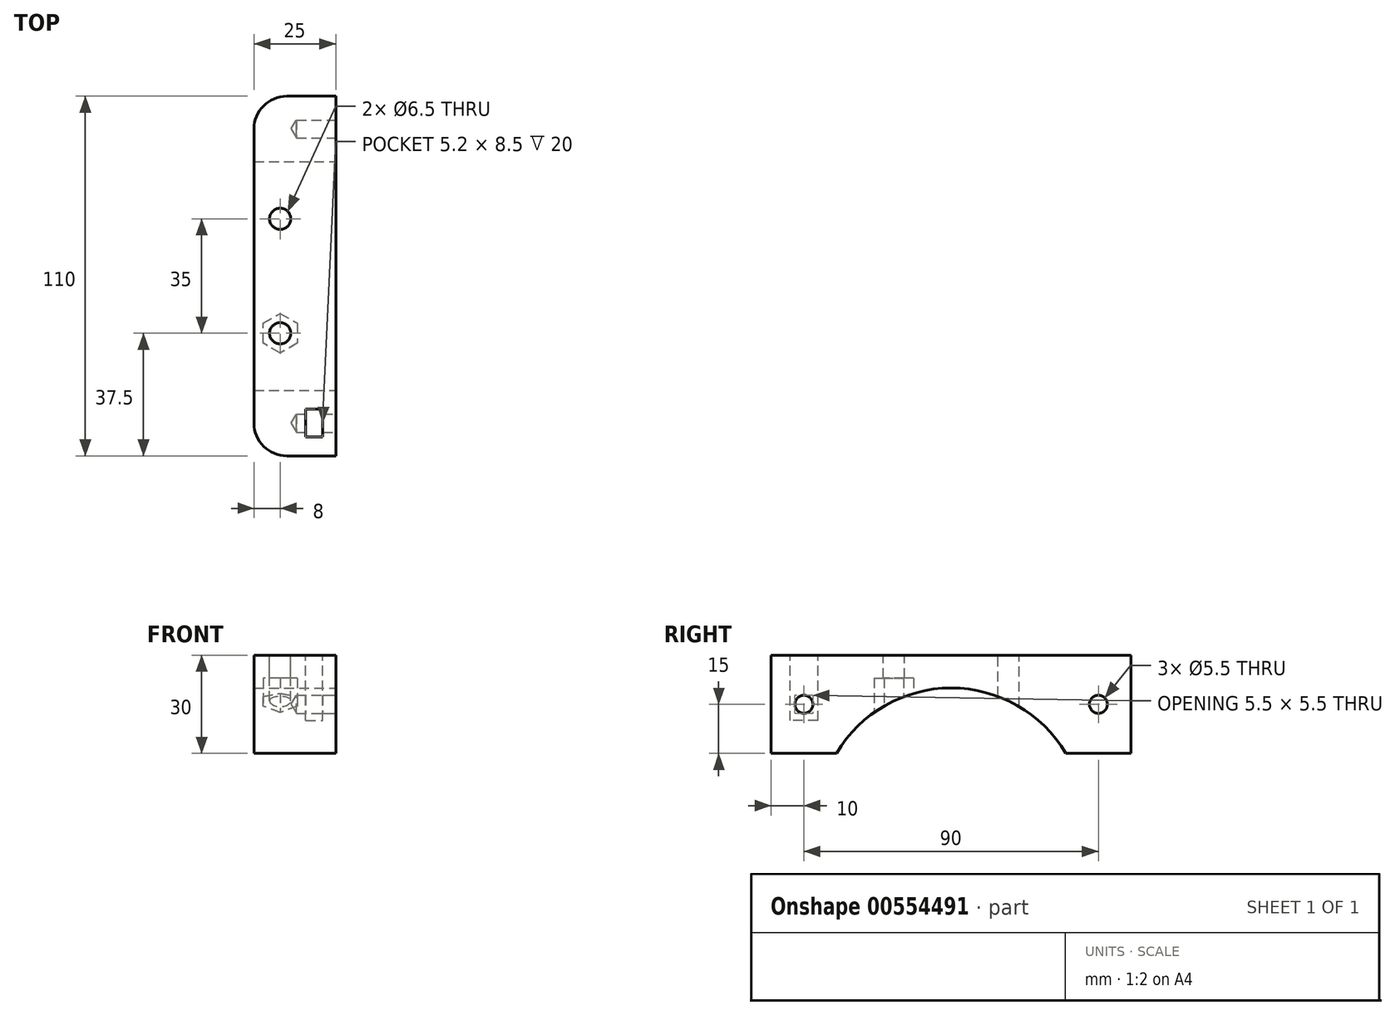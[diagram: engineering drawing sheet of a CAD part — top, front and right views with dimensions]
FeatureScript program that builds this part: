
annotation { "Feature Type Name" : "Feature", "Feature Type Description" : "" }
export const myFeature = defineFeature(function(context is Context, id is Id, definition is map)
    precondition{}
    {
        {
            var Q0;
            Q0=qCreatedBy(makeId("Right.planeOp"),FACE);
            var sketch = newSketch(context, id + "F0", { "sketchPlane" : qUnion([Q0])});
            skLineSegment(sketch, "E0.bottom", {"start": v(-55, 0) * mm, "end": v(55, 0) * mm});
            skLineSegment(sketch, "E0.top", {"start": v(-55, 30) * mm, "end": v(55, 30) * mm});
            skLineSegment(sketch, "E0.left", {"start": v(-55, 0) * mm, "end": v(-55, 30) * mm});
            skLineSegment(sketch, "E0.right", {"start": v(55, 0) * mm, "end": v(55, 30) * mm});
            skSolve(sketch);
        }
        {
            var Q0;
            Q0=makeQuery(id+"F0.imprint","IMPRINT",FACE,{"disambiguationData":[TD([[makeQuery(id+"F0.imprint","IMPRINT",EDGE,{"derivedFrom":sQuery(id+"F0.wireOp",EDGE,"E0.bottom")}),1.0]])]});
            extrude(context, id + "F1", {"entities" : qUnion([Q0]), "endBound" : BoundingType.SYMMETRIC, "depth" : 25 * mm, "offsetDistance" : 25 * mm});
        }
        {
            var Q0;
            Q0=makeQuery(id+"F1.opExtrude","CAP_FACE",FACE,{"disambiguationData":[OSD([sQuery(id+"F0.wireOp",EDGE,"E0.bottom"),sQuery(id+"F0.wireOp",EDGE,"E0.top"),sQuery(id+"F0.wireOp",EDGE,"E0.left"),sQuery(id+"F0.wireOp",EDGE,"E0.right")])],"isStart":false});
            var sketch = newSketch(context, id + "F2", { "sketchPlane" : qUnion([Q0])});
            skPoint(sketch, "E1", {"position": v(-45, 15) * mm});
            skPoint(sketch, "E2", {"position": v(45, 15) * mm});
            skSolve(sketch);
        }
        {
            var Q0;
            Q0=sQuery(id+"F2.wireOp",VERTEX,"E1");
            var Q1;
            Q1=sQuery(id+"F2.wireOp",VERTEX,"E2");
            var Q2;
            Q2=makeQuery(id+"F1.opExtrude","SWEPT_BODY",BODY,{"disambiguationData":[OSD([sQuery(id+"F0.wireOp",EDGE,"E0.bottom"),sQuery(id+"F0.wireOp",EDGE,"E0.top"),sQuery(id+"F0.wireOp",EDGE,"E0.left"),sQuery(id+"F0.wireOp",EDGE,"E0.right")])]});
            hole(context, id + "F3", {"style" : HoleStyle.SIMPLE, "endStyle" : HoleEndStyle.BLIND, "holeDiameter" : 5.5 * mm, "holeDepth" : 12 * mm, "isTappedThrough" : true, "tappedDepth" : 12 * mm, "tapClearance" : 3, "locations" : qUnion([Q0, Q1]), "scope" : qUnion([Q2])});
        }
        {
            var Q0;
            Q0=makeQuery(id+"F1.opExtrude","CAP_FACE",FACE,{"disambiguationData":[OSD([sQuery(id+"F0.wireOp",EDGE,"E0.bottom"),sQuery(id+"F0.wireOp",EDGE,"E0.top"),sQuery(id+"F0.wireOp",EDGE,"E0.left"),sQuery(id+"F0.wireOp",EDGE,"E0.right")])],"isStart":false});
            var sketch = newSketch(context, id + "F4", { "sketchPlane" : qUnion([Q0])});
            skArc(sketch, "E3", {"start": v(35, 0) * mm, "mid": v(0, 20) * mm, "end": v(-35, 0) * mm});
            skLineSegment(sketch, "E4", {"start": v(-35, 0) * mm, "end": v(35, 0) * mm});
            skSolve(sketch);
        }
        {
            var Q0;
            Q0=makeQuery(id+"F4.imprint","IMPRINT",FACE,{"disambiguationData":[TD([[makeQuery(id+"F4.imprint","IMPRINT",EDGE,{"derivedFrom":sQuery(id+"F4.wireOp",EDGE,"E3")}),1.0]])]});
            extrude(context, id + "F5", {"entities" : qUnion([Q0]), "operationType" : NewBodyOperationType.REMOVE, "endBound" : BoundingType.UP_TO_NEXT, "oppositeDirection" : true, "depth" : 25 * mm, "offsetDistance" : 25 * mm});
        }
        {
            var Q0;
            Q0=makeQuery(id+"F1.opExtrude","SWEPT_FACE",FACE,{"disambiguationData":[OSD([sQuery(id+"F0.wireOp",EDGE,"E0.top")])]});
            var sketch = newSketch(context, id + "F6", { "sketchPlane" : qUnion([Q0])});
            skPoint(sketch, "E5", {"position": v(-4.5, 17.5) * mm});
            skPoint(sketch, "E6", {"position": v(-4.5, -17.5) * mm});
            skSolve(sketch);
        }
        {
            var Q0;
            Q0=sQuery(id+"F6.wireOp",VERTEX,"E5");
            var Q1;
            Q1=sQuery(id+"F6.wireOp",VERTEX,"E6");
            var Q2;
            Q2=makeQuery(id+"F1.opExtrude","SWEPT_BODY",BODY,{"disambiguationData":[OSD([sQuery(id+"F0.wireOp",EDGE,"E0.bottom"),sQuery(id+"F0.wireOp",EDGE,"E0.top"),sQuery(id+"F0.wireOp",EDGE,"E0.left"),sQuery(id+"F0.wireOp",EDGE,"E0.right")])]});
            hole(context, id + "F7", {"style" : HoleStyle.SIMPLE, "endStyle" : HoleEndStyle.THROUGH, "holeDiameter" : 6.5 * mm, "isTappedThrough" : true, "tappedDepth" : 12 * mm, "tapClearance" : 3, "locations" : qUnion([Q0, Q1]), "scope" : qUnion([Q2])});
        }
        {
            var Q0;
            Q0=makeQuery(id+"F1.opExtrude","SWEPT_FACE",FACE,{"disambiguationData":[OSD([sQuery(id+"F0.wireOp",EDGE,"E0.top")])]});
            cPlane(context, id + "F8", {"entities" : qUnion([Q0]), "cplaneType" : CPlaneType.OFFSET, "offset" : 10 * mm, "oppositeDirection" : true, "width" : 150 * mm, "height" : 150 * mm});
        }
        {
            var Q0;
            Q0=qCreatedBy(id+"F8.planeOp",FACE);
            var sketch = newSketch(context, id + "F9", { "sketchPlane" : qUnion([Q0])});
            skCircle(sketch, "E7.cCircle", {"center": v(-4.5, -17.5) * mm, "radius": 5.25 * mm, "construction": true});
            skLineSegment(sketch, "E7.0", {"start": v(-4.5, -23.56) * mm, "end": v(-9.75, -20.53) * mm});
            skLineSegment(sketch, "E7.1", {"start": v(-9.75, -20.53) * mm, "end": v(-9.75, -14.47) * mm});
            skLineSegment(sketch, "E7.2", {"start": v(-9.75, -14.47) * mm, "end": v(-4.5, -11.44) * mm});
            skLineSegment(sketch, "E7.3", {"start": v(-4.5, -11.44) * mm, "end": v(0.75, -14.47) * mm});
            skLineSegment(sketch, "E7.4", {"start": v(0.75, -14.47) * mm, "end": v(0.75, -20.53) * mm});
            skLineSegment(sketch, "E7.5", {"start": v(0.75, -20.53) * mm, "end": v(-4.5, -23.56) * mm});
            skPoint(sketch, "E7.0.midPoint", {"position": v(-7.13, -22.05) * mm});
            skLineSegment(sketch, "E8", {"start": v(-12.5, 0) * mm, "end": v(12.5, 0) * mm});
            skSolve(sketch);
        }
        {
            var Q0;
            Q0 = qSketchRegion(id + "F9", true);
            extrude(context, id + "F10", {"entities" : qUnion([Q0]), "operationType" : NewBodyOperationType.REMOVE, "depth" : 3 * mm, "offsetDistance" : 25 * mm, "hasSecondDirection" : true, "secondDirectionBound" : SecondDirectionBoundingType.THROUGH_ALL, "secondDirectionOppositeDirection" : true, "secondDirectionDepth" : 25 * mm});
        }
        {
            var Q0;
            Q0=makeQuery(id+"F1.opExtrude","SWEPT_FACE",FACE,{"disambiguationData":[OSD([sQuery(id+"F0.wireOp",EDGE,"E0.top")])]});
            var sketch = newSketch(context, id + "F11", { "sketchPlane" : qUnion([Q0])});
            skLineSegment(sketch, "E9.bottom", {"start": v(3.3, -40.75) * mm, "end": v(8.5, -40.75) * mm});
            skLineSegment(sketch, "E9.top", {"start": v(3.3, -49.25) * mm, "end": v(8.5, -49.25) * mm});
            skLineSegment(sketch, "E9.left", {"start": v(3.3, -40.75) * mm, "end": v(3.3, -49.25) * mm});
            skLineSegment(sketch, "E9.right", {"start": v(8.5, -40.75) * mm, "end": v(8.5, -49.25) * mm});
            skPoint(sketch, "E10", {"position": v(8.5, -45) * mm});
            skSolve(sketch);
        }
        {
            var Q0;
            Q0=makeQuery(id+"F11.imprint","IMPRINT",FACE,{"disambiguationData":[TD([[makeQuery(id+"F11.imprint","IMPRINT",EDGE,{"derivedFrom":sQuery(id+"F11.wireOp",EDGE,"E9.bottom")}),-1.0]])]});
            extrude(context, id + "F12", {"entities" : qUnion([Q0]), "operationType" : NewBodyOperationType.REMOVE, "oppositeDirection" : true, "depth" : 20 * mm, "offsetDistance" : 25 * mm});
        }
        {
            var Q0;
            Q0=makeQuery(id+"F1.opExtrude","CAP_EDGE",EDGE,{"disambiguationData":[OSD([sQuery(id+"F0.wireOp",EDGE,"E0.left")])],"isStart":true});
            var Q1;
            Q1=makeQuery(id+"F1.opExtrude","CAP_EDGE",EDGE,{"disambiguationData":[OSD([sQuery(id+"F0.wireOp",EDGE,"E0.right")])],"isStart":true});
            fillet(context, id + "F13", {"entities" : qUnion([Q0, Q1]), "radius" : 10 * mm, "tangentPropagation" : true, "allowEdgeOverflow" : false});
        }
    });
